# Revit family: Storage-Teknion-EMCM_Medium_Single_Cabinet-R2016
name_source: partatom
category: Furniture
revit_build: Autodesk Revit 2018 (Build: 20190510_1515(x64)
units: mm (PartAtom-declared; Revit-internal decimal feet)

## family parameters
Always vertical = Yes
Cut with Voids When Loaded = No
OmniClass Number = 23.40.20.00
OmniClass Title = General Furniture and Specialties
Room Calculation Point = No
Shared = Yes
Work Plane-Based = No

## types (7) — shared parameters
Assembly Code = E2020200
Manufacturer = Teknion
Manufacturer Fax = 416.661.4586
Part Number = EMCM
Product Documentation Link = https://assets.teknion.com
Product Line = Emote
Product Page URL = https://www.teknion.com
Series = Emote
Sustainability Data = https://www.teknion.com
URL = www.teknion.com
Unit Weight URL = http://www.teknion.com
Warranty = http://www.teknion.com

## per-type parameters (varying)
| type | Bottom Cabinet Height | Bottom Cabinet Horizontal Pull Visibility | Bottom Cabinet Visibility | Bottom of 2 Drawers Cut Hole Depth | Bottom of Top Cabinet Height Offset | Description | Double Door Cut Hole Depth | Drawer 2d Masking Region Visibility | Model | Open | Second Shelf Visibility | Top Cabinet Height | Top Cabinet Visibility | Two Handle Height and Cut Height Offset | Two Handle Visiblity |
| Partial Height Drawer | 13 " | Yes | Yes | 0 " | 20.779 " | Emote Medium Single Cabinet, Partial Height Drawer, 29" Width, 45" Height | 0.5 " | Yes | EMCMPD2945 | No | Yes | 33.8 " | No | 20.7 " | No |
| Open | 17.25 " | No | No | 0 " | 25.029 " | Emote Medium Single Cabinet, Open, 29" Width, 45" Height | 0.5 " | No | EMCMOP2945 | Yes | Yes | 33.8 " | No | 24.95 " | No |
| Full Height Drawer | 17.25 " | Yes | Yes | 0 " | 25.029 " | Emote Medium Single Cabinet, Full Height Drawer, 29" Width, 45" Height | 0.5 " | Yes | EMCMFD2945 | No | Yes | 37.7 " | No | 24.95 " | No |
| Lower Closed | 17.25 " | No | Yes | 0 " | 25.029 " | Emote Medium Single Cabinet, Lower Closed, 29" Width, 45" Height | 0.5 " | Yes | EMCMLC2945 | No | Yes | 37.7 " | No | 24.95 " | Yes |
| Double Drawers | 13 " | Yes | Yes | 0 " | 20.779 " | Emote Medium Single Cabinet, Double Drawers, 29" Width, 45" Height | 0.5 " | Yes | EMCMDD2945 | No | Yes | 33.8 " | Yes | 20.7 " | No |
| Double Doors | 13 " | No | No | 0 " | 7.7 " | Emote Medium Single Cabinet, Double Doors, 29" Width, 45" Height | 3 " | Yes | EMCMDD2945 | No | No | 41.447 " | Yes | 41.447 " | Yes |
| Drawer/Double Doors Combo | 17.25 " | Yes | Yes | 17.329 " | 25.029 " | Emote Medium Single Cabinet, Drawer/Double Doors Combo, 29" Width, 45" Height | 0.5 " | Yes | EMCMDC2945 | No | No | 41.447 " | Yes | 41.447 " | Yes |

type visibility flags (boolean, named after types; folded from table):
- Partial Height Drawer: Yes: Partial Height Drawer
- Open: Yes: (none)
- Full Height Drawer: Yes: Full Height Drawer
- Lower Closed: Yes: Lower Closed
- Double Drawers: Yes: Double Drawers
- Double Doors: Yes: Double Doors
- Drawer/Double Doors Combo: Yes: Drawer/Double Doors Combo

## geometry (parser evidence)
native form markers: Blend x31, Sweep x1
no freeform markers — native parametric forms only
